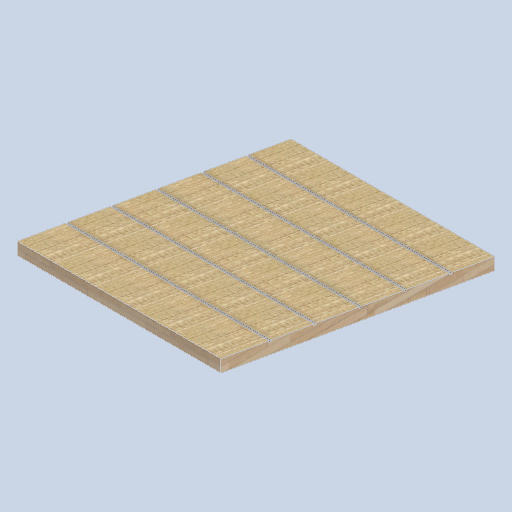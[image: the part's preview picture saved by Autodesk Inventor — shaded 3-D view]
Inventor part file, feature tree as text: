
AUTODESK INVENTOR PART (.ipt)
format: ipt  version: 2024.2 (Build 282272000, 272)  size: 256,000 bytes
history: native  units: in
note: dims shown in document units (in); Inventor stores cm internally (conversion verified against a paired STEP export)
features: sketch x5, other x3, plane x3
ambient origin geometry x8: Origin, YZ Plane, XZ Plane, XY Plane, X Axis, Y Axis, Z Axis, Center Point
bodies: Solid1 (feature_tree)
feature tree (11):
  other  "eave_panel_02.ipt"
  other  "Solid1::eave_panel_02.ipt"
  other  "TaggingFeature1"
  sketch  "Sketch1"  dims[d0=0.3937in]
  sketch  "Sketch2"
  sketch  "Sketch3"
  sketch  "Sketch4"
  sketch  "Sketch5"
  plane  "Work Plane1"
  plane  "Work Plane2"
  plane  "Work Plane3"
